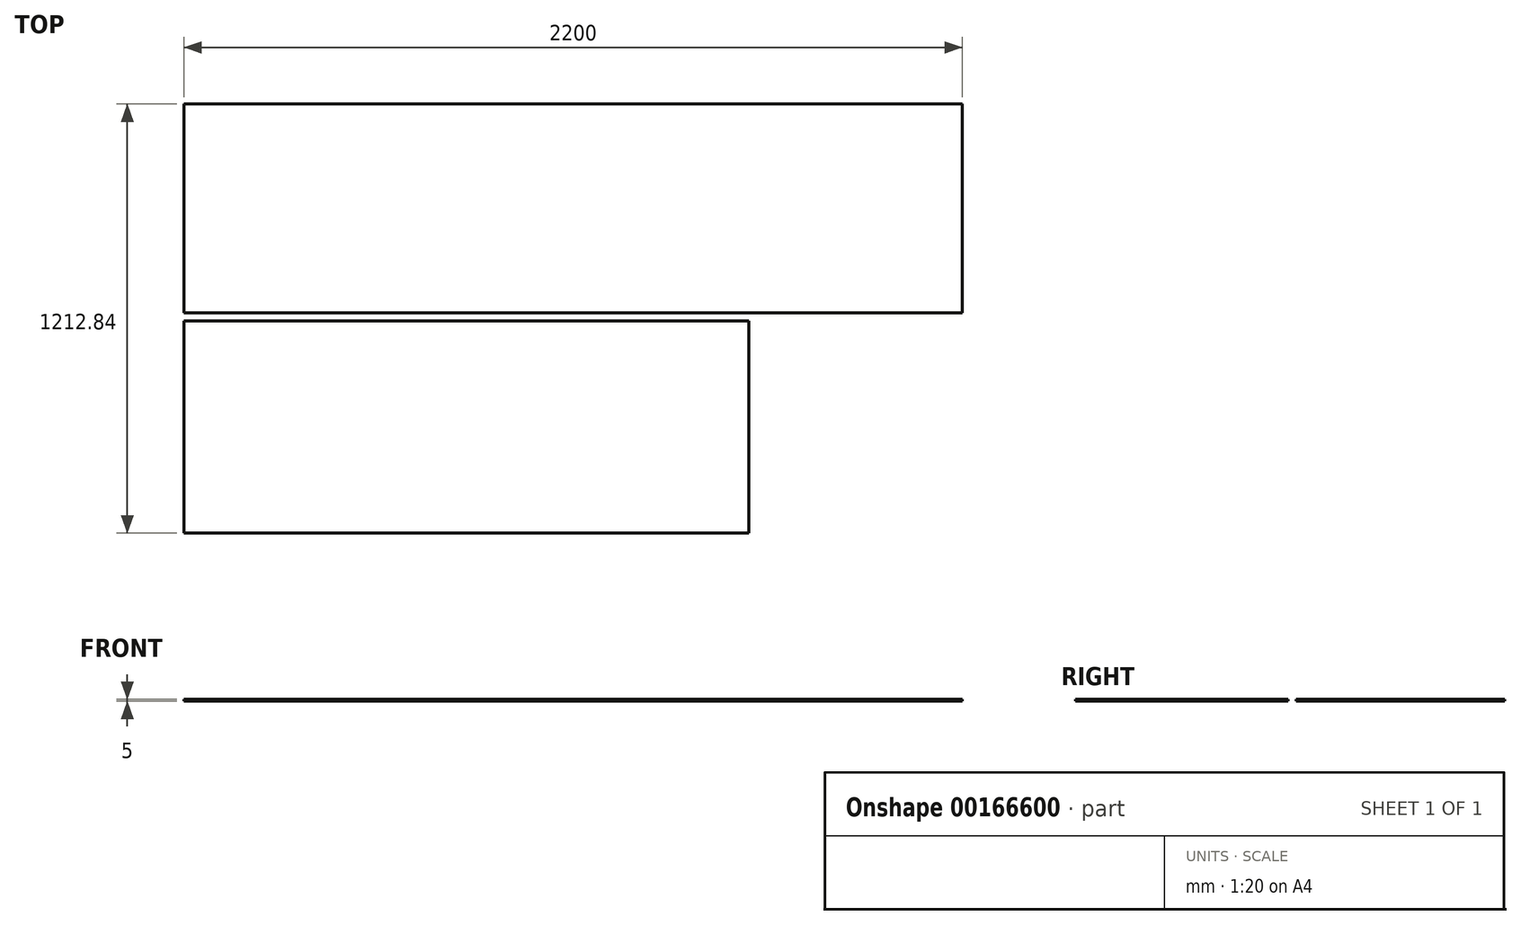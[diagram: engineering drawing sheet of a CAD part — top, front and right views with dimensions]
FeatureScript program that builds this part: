
annotation { "Feature Type Name" : "Feature", "Feature Type Description" : "" }
export const myFeature = defineFeature(function(context is Context, id is Id, definition is map)
    precondition{}
    {
        {
            var Q0;
            Q0=qCreatedBy(makeId("Top.planeOp"),FACE);
            var sketch = newSketch(context, id + "F0", { "sketchPlane" : qUnion([Q0])});
            skLineSegment(sketch, "E0.bottom", {"start": v(798, -300) * mm, "end": v(-798, -300) * mm});
            skLineSegment(sketch, "E0.top", {"start": v(798, 300) * mm, "end": v(-798, 300) * mm});
            skLineSegment(sketch, "E0.left", {"start": v(798, -300) * mm, "end": v(798, 300) * mm});
            skLineSegment(sketch, "E0.right", {"start": v(-798, -300) * mm, "end": v(-798, 300) * mm});
            skPoint(sketch, "E0.middle", {"position": v(0, 0) * mm});
            skLineSegment(sketch, "E1.bottom", {"start": v(-798, 322.84) * mm, "end": v(1402, 322.84) * mm});
            skLineSegment(sketch, "E1.top", {"start": v(-798, 912.84) * mm, "end": v(1402, 912.84) * mm});
            skLineSegment(sketch, "E1.left", {"start": v(-798, 322.84) * mm, "end": v(-798, 912.84) * mm});
            skLineSegment(sketch, "E1.right", {"start": v(1402, 322.84) * mm, "end": v(1402, 912.84) * mm});
            skSolve(sketch);
        }
        {
            var Q0;
            Q0=qSketchRegion(id+"F0",true);
            extrude(context, id + "F1", {"entities" : qUnion([Q0]), "depth" : 5 * mm});
        }
    });
